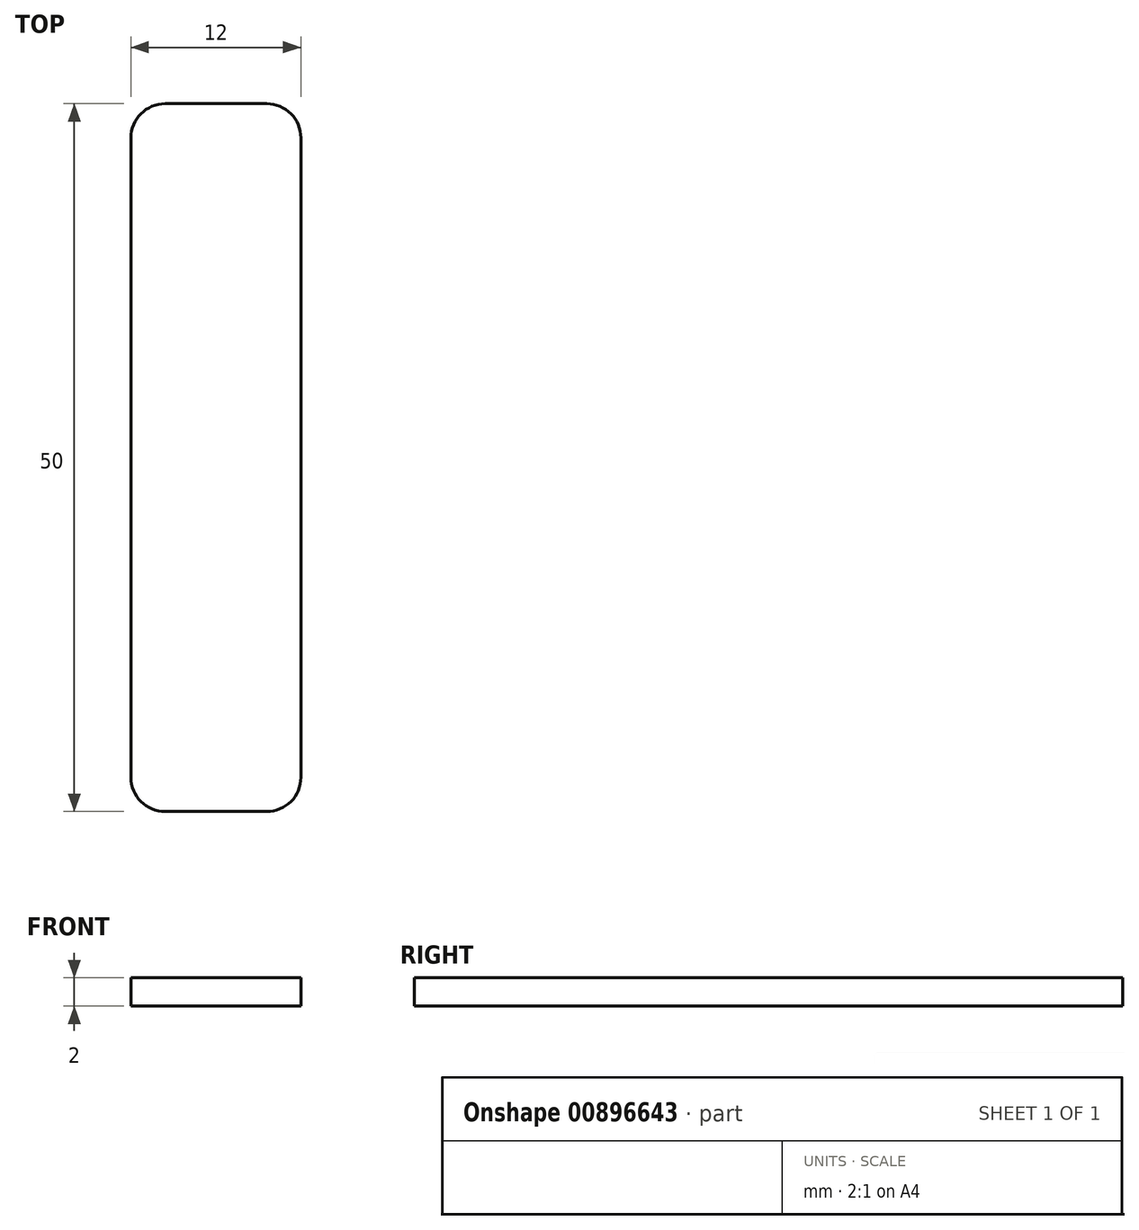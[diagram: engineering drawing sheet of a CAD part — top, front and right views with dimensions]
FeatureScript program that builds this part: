
annotation { "Feature Type Name" : "Feature", "Feature Type Description" : "" }
export const myFeature = defineFeature(function(context is Context, id is Id, definition is map)
    precondition{}
    {
        {
            var Q0;
            Q0=qCreatedBy(makeId("Top.planeOp"),FACE);
            var sketch = newSketch(context, id + "F0", { "sketchPlane" : qUnion([Q0])});
            skLineSegment(sketch, "E0.bottom", {"start": v(-6.58, 22.36) * mm, "end": v(5.42, 22.36) * mm});
            skLineSegment(sketch, "E0.top", {"start": v(-6.58, -27.64) * mm, "end": v(5.42, -27.64) * mm});
            skLineSegment(sketch, "E0.left", {"start": v(-6.58, 22.36) * mm, "end": v(-6.58, -27.64) * mm});
            skLineSegment(sketch, "E0.right", {"start": v(5.42, 22.36) * mm, "end": v(5.42, -27.64) * mm});
            skSolve(sketch);
        }
        {
            var Q0;
            Q0 = qSketchRegion(id + "F0", true);
            var Q1;
            Q1=makeQuery(id+"F0.imprint","IMPRINT",FACE,{"disambiguationData":[TD([[makeQuery(id+"F0.imprint","IMPRINT",EDGE,{"derivedFrom":sQuery(id+"F0.wireOp",EDGE,"E0.bottom")}),-1.0]])]});
            extrude(context, id + "F1", {"entities" : qUnion([Q0, Q1]), "depth" : 2 * mm, "offsetDistance" : 25 * mm});
        }
        {
            var Q0;
            Q0=makeQuery(id+"F1.opExtrude","SWEPT_EDGE",EDGE,{"disambiguationData":[OSD([sQuery(id+"F0.wireOp",EDGE,"E0.top"),sQuery(id+"F0.wireOp",EDGE,"E0.left")])]});
            var Q1;
            Q1=makeQuery(id+"F1.opExtrude","SWEPT_EDGE",EDGE,{"disambiguationData":[OSD([sQuery(id+"F0.wireOp",EDGE,"E0.top"),sQuery(id+"F0.wireOp",EDGE,"E0.right")])]});
            var Q2;
            Q2=makeQuery(id+"F1.opExtrude","SWEPT_EDGE",EDGE,{"disambiguationData":[OSD([sQuery(id+"F0.wireOp",EDGE,"E0.bottom"),sQuery(id+"F0.wireOp",EDGE,"E0.right")])]});
            var Q3;
            Q3=makeQuery(id+"F1.opExtrude","SWEPT_EDGE",EDGE,{"disambiguationData":[OSD([sQuery(id+"F0.wireOp",EDGE,"E0.bottom"),sQuery(id+"F0.wireOp",EDGE,"E0.left")])]});
            fillet(context, id + "F2", {"entities" : qUnion([Q0, Q1, Q2, Q3]), "radius" : 2.41 * mm, "tangentPropagation" : true, "allowEdgeOverflow" : false});
        }
    });
